# Revit family: Power-ModularDevices-GEWISS-90AM-BUZZER_TRANSFORMER
name_source: partatom
category: Apparecchi elettrici
revit_build: Autodesk Revit 2016 (Build: 20161004_0715(x64)
units: mm (PartAtom-declared; Revit-internal decimal feet)

## family parameters
Condiviso = No
Host = Superficie
Mantenere orientamento annotazione = Sì
Numero OmniClass = 23.80.50.00
Punto di calcolo locali = Sì
Quota connettore circolare = Usa diametro
Taglio con vuoti quando caricato = No
Tipo di parte = Normale
Titolo OmniClass = Terminals for Power Supply

## types (1)
- GW96408 - BUZZER 230V AC 2M. WITH TRANSFORMER
    Catalogue = POWER
    Catalogue Range = 90 AM
    Descrizione = BUZZER 230V AC 2M. WITH TRANSFORMER
    EAN code = 8011564063686
    Electrocod = 140
    IDF = 296c82ce-8426-478b-b711-23f7297921be
    IDT = 2f51bfe9-bcf0-469b-8fdd-40b6c8d623b3
    Immagine tipo = GW96408.jpg
    Modello = GW96408
    No. Chorus modules = 2
    No. of modules EN 50022 = 2
    Numero di poli = 1
    Power loss = 6,1VA
    Produttore = GEWISS S.p.A.
    Prospetto di default = 1219 mm
    Rated voltage = 230V
    SEO = Buzzer
    Technical sheet = https://www.gewiss.com
    URL = https://www.gewiss.com
    Version file RFA = 18.0
    carico = Altro
    potenza in watt = 0 V
